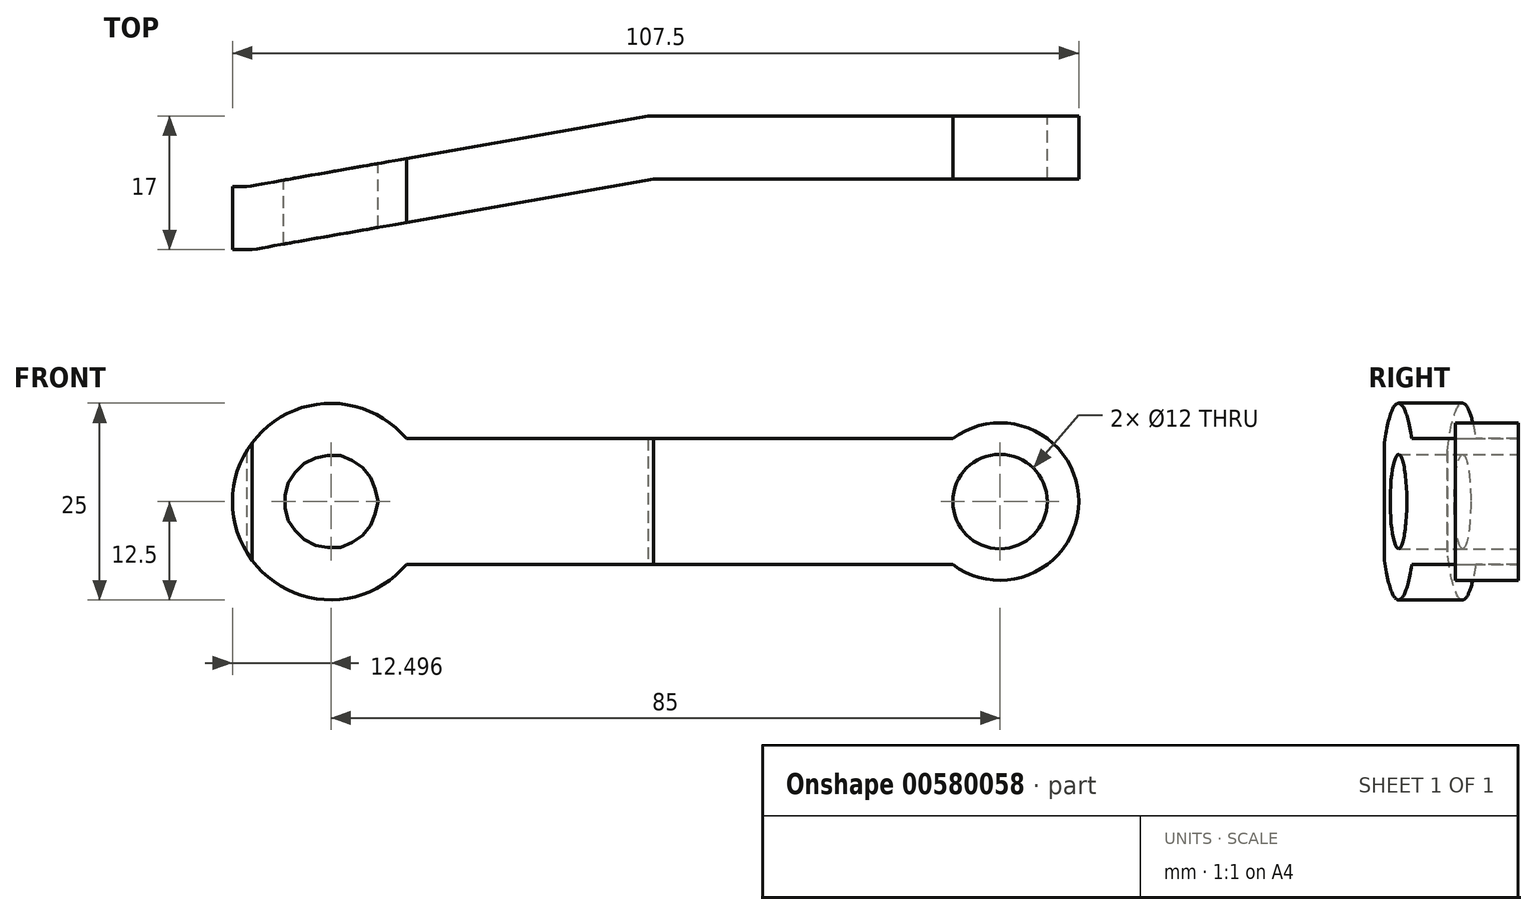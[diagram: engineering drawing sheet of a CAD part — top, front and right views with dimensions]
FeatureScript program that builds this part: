
annotation { "Feature Type Name" : "Feature", "Feature Type Description" : "" }
export const myFeature = defineFeature(function(context is Context, id is Id, definition is map)
    precondition{}
    {
        {
            var Q0;
            Q0=qCreatedBy(makeId("Front.planeOp"),FACE);
            var sketch = newSketch(context, id + "F0", { "sketchPlane" : qUnion([Q0])});
            skCircle(sketch, "E0", {"center": v(-40.31, 0) * mm, "radius": 12.5 * mm});
            skCircle(sketch, "E1", {"center": v(44.69, 0) * mm, "radius": 10 * mm});
            skLineSegment(sketch, "E2", {"start": v(-30.7, 8) * mm, "end": v(38.69, 8) * mm});
            skLineSegment(sketch, "E3.MirrorCS", {"start": v(-30.7, -8) * mm, "end": v(38.69, -8) * mm});
            skCircle(sketch, "E4", {"center": v(-40.31, 0) * mm, "radius": 6 * mm});
            skCircle(sketch, "E5", {"center": v(44.69, 0) * mm, "radius": 6 * mm});
            skSolve(sketch);
        }
        {
            var Q0;
            Q0=makeQuery(id+"F0.imprint","IMPRINT",FACE,{"disambiguationData":[TD([[makeQuery(id+"F0.imprint","IMPRINT",EDGE,{"derivedFrom":sQuery(id+"F0.wireOp",EDGE,"E4")}),-1.0]])]});
            var Q1;
            {var subQ0=sQuery(id+"F0.wireOp",EDGE,"E2");Q1=makeQuery(id+"F0.imprint","IMPRINT",FACE,{"disambiguationData":[TD([[makeQuery(id+"F0.imprint","IMPRINT",EDGE,{"derivedFrom":subQ0}),-1.0]])]});}
            var Q2;
            Q2=makeQuery(id+"F0.imprint","IMPRINT",FACE,{"disambiguationData":[TD([[makeQuery(id+"F0.imprint","IMPRINT",EDGE,{"derivedFrom":sQuery(id+"F0.wireOp",EDGE,"E5")}),-1.0]])]});
            extrude(context, id + "F1", {"entities" : qUnion([Q0, Q1, Q2]), "depth" : 25 * mm, "offsetDistance" : 25 * mm});
        }
        {
            var Q0;
            Q0=qCreatedBy(makeId("Top.planeOp"),FACE);
            var sketch = newSketch(context, id + "F2", { "sketchPlane" : qUnion([Q0])});
            skLineSegment(sketch, "E6", {"start": v(-52.81, -9) * mm, "end": v(-51.04, -9) * mm});
            skLineSegment(sketch, "E7", {"start": v(-51.04, -9) * mm, "end": v(0, 0) * mm});
            skLineSegment(sketch, "E8", {"start": v(25.57, 0) * mm, "end": v(54.69, 0) * mm});
            skLineSegment(sketch, "E9.0", {"start": v(0.7, -8) * mm, "end": v(54.69, -8) * mm});
            skLineSegment(sketch, "E9.1", {"start": v(-50.34, -17) * mm, "end": v(0.7, -8) * mm});
            skLineSegment(sketch, "E9.2", {"start": v(-52.81, -17) * mm, "end": v(-50.34, -17) * mm});
            skPoint(sketch, "E10", {"position": v(45.57, 0) * mm});
            skLineSegment(sketch, "E11", {"start": v(0, 0) * mm, "end": v(25.57, 0) * mm});
            skLineSegment(sketch, "E12", {"start": v(-52.81, -25) * mm, "end": v(-52.81, 0) * mm});
            skLineSegment(sketch, "E13", {"start": v(54.69, 0) * mm, "end": v(54.69, -25) * mm});
            skSolve(sketch);
        }
        {
            var Q0;
            Q0=qSketchRegion(id+"F2",true);
            extrude(context, id + "F3", {"entities" : qUnion([Q0]), "operationType" : NewBodyOperationType.INTERSECT, "endBound" : BoundingType.SYMMETRIC, "depth" : 25 * mm, "offsetDistance" : 25 * mm});
        }
    });
